# Revit family: LTC-3SQD-W
name_source: partatom
category: Lighting Fixtures
revit_build: Autodesk Revit 2014 (Build: 20130308_1515(x64)
units: mm (PartAtom-declared; Revit-internal decimal feet)

## types (1)
- LTC-3SQD-W
    Apparent Load = 72 VA
    Backbox = Hubbell - Matt Black
    Ballast = Paint - Hubbell - Carbon Black
    Certifications = • cCSAus certified to UL 1598
• Wall Mount: Suitable for wet locations
• Surface & Pendant Mount: Suitable for wet
locations under covered ceiling
• Cord Mount and all Wall Wash: Suitable for
damp locations
    Color Filter = 16777215
    Default Elevation = 48 "
    Description = LITEISTRY™ 3inch Square Cylinder
    Dimming Lamp Color Temperature Shift = <None>
    Emit Shape Visible in Rendering = No
    Emit from Rectangle Length = 4 "
    Emit from Rectangle Width = 4 "
    Features = •	3inch architectural LED square downlight and wall wash cylinder delivering 600 - 2000 lm
•	4 beam distributions from 0.6 to 1.2 Spacing Criteria
•	Quiet reflector appearance with 50º optical cutoff
•	2700K - 5000K, 80+ and 90+ CRI options
•	Available in Surface, Wall, Pendant, or Cord Mount configurations
•	Variety of dimming protocol options including 0-10V, DALI, DMX, Forward Phase and EcoSystem
•	NX Distributed Intelligence™ wired and wireless controls capability available
•	2 SDCM color consistency
•	Long life L90 at 55,000 hrs (TM-21)
•	Five year warranty
    Lamp = LED Lamp
    Manufacturer = Prescolite
    Model = LTC-3SQD
    Photometric Web File = LTC-3SQD-P-20L35K8MD-DM1-S-BL.ies
    Product Documentation Link = https://hubbellcdn.com
    Product Page URL = https://www.hubbell.com
    Reflector = Glass - Hubbell - Glass
    Tilt Angle = -90.00°
    URL = http://www.prescolite.com
    Voltage = 120 V
    Warranty = • 5 year warranty
• See HLI Standard Warranty for
additional information
    Wattage Comments = 8-25W

## geometry (parser evidence)
native form markers: Blend x12, Sweep x3
no freeform markers — native parametric forms only
